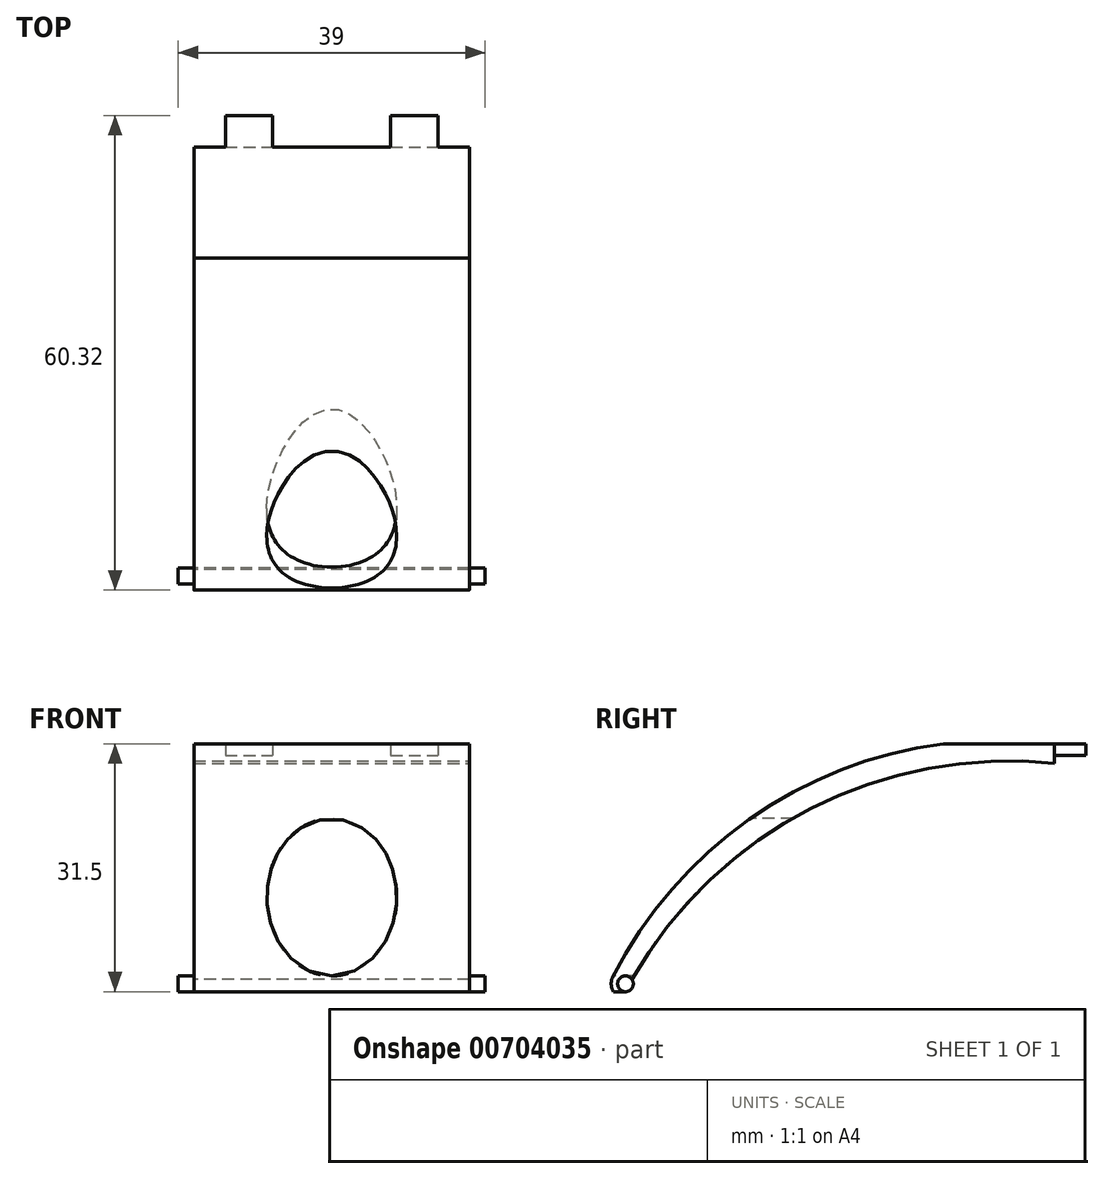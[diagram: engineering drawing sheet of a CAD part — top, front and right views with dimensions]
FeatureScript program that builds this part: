
annotation { "Feature Type Name" : "Feature", "Feature Type Description" : "" }
export const myFeature = defineFeature(function(context is Context, id is Id, definition is map)
    precondition{}
    {
        {
            var Q0;
            Q0=qCreatedBy(makeId("Top.planeOp"),FACE);
            var sketch = newSketch(context, id + "F0", { "sketchPlane" : qUnion([Q0])});
            skLineSegment(sketch, "E0.bottom", {"start": v(-17.4, 3.7) * mm, "end": v(17.6, 3.7) * mm});
            skLineSegment(sketch, "E0.top", {"start": v(-17.4, -53.3) * mm, "end": v(17.6, -53.3) * mm});
            skLineSegment(sketch, "E0.left", {"start": v(-17.4, 3.7) * mm, "end": v(-17.4, -53.3) * mm});
            skLineSegment(sketch, "E0.right", {"start": v(17.6, 3.7) * mm, "end": v(17.6, -53.3) * mm});
            skSolve(sketch);
        }
        {
            var Q0;
            Q0=makeQuery(id+"F0.imprint","IMPRINT",FACE,{"disambiguationData":[TD([[makeQuery(id+"F0.imprint","IMPRINT",EDGE,{"derivedFrom":sQuery(id+"F0.wireOp",EDGE,"E0.bottom")}),-1.0]])]});
            extrude(context, id + "F1", {"entities" : qUnion([Q0]), "depth" : 31.5 * mm, "offsetDistance" : 25 * mm});
        }
        {
            var Q0;
            Q0=makeQuery(id+"F1.opExtrude","SWEPT_FACE",FACE,{"disambiguationData":[OSD([sQuery(id+"F0.wireOp",EDGE,"E0.right")])]});
            var sketch = newSketch(context, id + "F2", { "sketchPlane" : qUnion([Q0])});
            skArc(sketch, "E1", {"start": v(3.7, 31.5) * mm, "mid": v(-29.97, 25.1) * mm, "end": v(-53.3, 0) * mm});
            skSolve(sketch);
        }
        {
            var Q0;
            Q0=makeQuery(id+"F1.opExtrude","SWEPT_FACE",FACE,{"disambiguationData":[OSD([sQuery(id+"F0.wireOp",EDGE,"E0.top")])]});
            var sketch = newSketch(context, id + "F3", { "sketchPlane" : qUnion([Q0])});
            skEllipse(sketch, "E2", {"center": v(0.1, 12) * mm, "majorRadius": 10 * mm, "minorRadius": 8.25 * mm, "majorAxis": v(0, -1)});
            skSolve(sketch);
        }
        {
            var Q0;
            Q0=makeQuery(id+"F3.imprint","IMPRINT",FACE,{"disambiguationData":[TD([[makeQuery(id+"F3.imprint","IMPRINT",EDGE,{"derivedFrom":sQuery(id+"F3.wireOp",EDGE,"E2")}),1.0]])]});
            extrude(context, id + "F4", {"entities" : qUnion([Q0]), "operationType" : NewBodyOperationType.REMOVE, "endBound" : BoundingType.THROUGH_ALL, "oppositeDirection" : true, "depth" : 25 * mm, "offsetDistance" : 25 * mm});
        }
        {
            var Q0;
            Q0=makeQuery(id+"F2.imprint","IMPRINT",FACE,{"disambiguationData":[TD([[makeQuery(id+"F2.imprint","IMPRINT",EDGE,{"derivedFrom":sQuery(id+"F2.wireOp",EDGE,"E1")}),-1.0]])]});
            extrude(context, id + "F5", {"entities" : qUnion([Q0]), "operationType" : NewBodyOperationType.REMOVE, "endBound" : BoundingType.THROUGH_ALL, "oppositeDirection" : true, "depth" : 25 * mm, "offsetDistance" : 25 * mm});
        }
        {
            var Q0;
            Q0=makeQuery(id+"F1.opExtrude","SWEPT_FACE",FACE,{"disambiguationData":[OSD([sQuery(id+"F0.wireOp",EDGE,"E0.right")])]});
            var sketch = newSketch(context, id + "F6", { "sketchPlane" : qUnion([Q0])});
            skArc(sketch, "E3", {"start": v(3.7, 29) * mm, "mid": v(-28, 22.87) * mm, "end": v(-50.8, 0) * mm});
            skSolve(sketch);
        }
        {
            var Q0;
            {var subQ0=sQuery(id+"F6.wireOp",EDGE,"E3");Q0=makeQuery(id+"F6.imprint","IMPRINT",FACE,{"disambiguationData":[TD([[makeQuery(id+"F6.imprint","IMPRINT",EDGE,{"derivedFrom":subQ0}),1.0]])]});}
            extrude(context, id + "F7", {"entities" : qUnion([Q0]), "operationType" : NewBodyOperationType.REMOVE, "endBound" : BoundingType.THROUGH_ALL, "oppositeDirection" : true, "depth" : 25 * mm, "offsetDistance" : 25 * mm});
        }
        {
            var Q0;
            Q0=makeQuery(id+"F1.opExtrude","SWEPT_FACE",FACE,{"disambiguationData":[OSD([sQuery(id+"F0.wireOp",EDGE,"E0.right")])]});
            var sketch = newSketch(context, id + "F8", { "sketchPlane" : qUnion([Q0])});
            skCircle(sketch, "E4", {"center": v(-50.8, 1) * mm, "radius": 1 * mm});
            skSolve(sketch);
        }
        {
            var Q0;
            {var subQ0=sQuery(id+"F8.wireOp",EDGE,"E4");var subQ1=makeQuery(id+"F7.boolean.opBoolean","COPY",EDGE,{"derivedFrom":makeQuery(id+"F7.opExtrude","CAP_EDGE",EDGE,{"disambiguationData":[OSD([sQuery(id+"F6.wireOp",EDGE,"E3")])],"isStart":true})});var subQ3=makeQuery(id+"F8.imprint","INTERSECT",VERTEX,{"derivedFrom":[subQ1,subQ0]});Q0=makeQuery(id+"F8.imprint","IMPRINT",FACE,{"disambiguationData":[TD([[makeQuery(id+"F8.imprint","IMPRINT",EDGE,{"disambiguationData":[TD([[subQ3,-1.0]])],"derivedFrom":subQ0}),1.0]])]});}
            var Q1;
            {var subQ0=sQuery(id+"F8.wireOp",EDGE,"E4");var subQ1=makeQuery(id+"F7.boolean.opBoolean","COPY",EDGE,{"derivedFrom":makeQuery(id+"F7.opExtrude","CAP_EDGE",EDGE,{"disambiguationData":[OSD([sQuery(id+"F6.wireOp",EDGE,"E3")])],"isStart":true})});var subQ3=makeQuery(id+"F8.imprint","INTERSECT",VERTEX,{"derivedFrom":[subQ1,subQ0]});Q1=makeQuery(id+"F8.imprint","IMPRINT",FACE,{"disambiguationData":[TD([[makeQuery(id+"F8.imprint","IMPRINT",EDGE,{"disambiguationData":[TD([[subQ3,1.0]])],"derivedFrom":subQ0}),1.0]])]});}
            extrude(context, id + "F9", {"entities" : qUnion([Q0, Q1]), "operationType" : NewBodyOperationType.ADD, "depth" : 2 * mm, "offsetDistance" : 25 * mm, "hasSecondDirection" : true, "secondDirectionOppositeDirection" : true, "secondDirectionDepth" : 37 * mm});
        }
        {
            var Q0;
            Q0=makeQuery(id+"F1.opExtrude","SWEPT_FACE",FACE,{"disambiguationData":[OSD([sQuery(id+"F0.wireOp",EDGE,"E0.right")])]});
            var sketch = newSketch(context, id + "F10", { "sketchPlane" : qUnion([Q0])});
            skCircle(sketch, "E5", {"center": v(-50.8, 1) * mm, "radius": 1.82 * mm});
            skSolve(sketch);
        }
        {
            var Q0;
            {var subQ0=sQuery(id+"F10.wireOp",EDGE,"E5");var subQ1=makeQuery(id+"F5.boolean.opBoolean","COPY",EDGE,{"derivedFrom":makeQuery(id+"F5.opExtrude","CAP_EDGE",EDGE,{"disambiguationData":[OSD([sQuery(id+"F2.wireOp",EDGE,"E1")])],"isStart":true})});var subQ2=makeQuery(id+"F10.imprint","INTERSECT",VERTEX,{"derivedFrom":[subQ1,subQ0]});Q0=makeQuery(id+"F10.imprint","IMPRINT",FACE,{"disambiguationData":[TD([[makeQuery(id+"F10.imprint","IMPRINT",EDGE,{"disambiguationData":[TD([[subQ2,-1.0]])],"derivedFrom":subQ0}),-1.0]])]});}
            extrude(context, id + "F11", {"entities" : qUnion([Q0]), "operationType" : NewBodyOperationType.REMOVE, "endBound" : BoundingType.THROUGH_ALL, "oppositeDirection" : true, "depth" : 25 * mm, "offsetDistance" : 25 * mm});
        }
        {
            var Q0;
            Q0=makeQuery(id+"F1.opExtrude","SWEPT_FACE",FACE,{"disambiguationData":[OSD([sQuery(id+"F0.wireOp",EDGE,"E0.bottom")])]});
            var sketch = newSketch(context, id + "F12", { "sketchPlane" : qUnion([Q0])});
            skLineSegment(sketch, "E6.bottom", {"start": v(-13.6, 31.5) * mm, "end": v(-7.6, 31.5) * mm});
            skLineSegment(sketch, "E6.top", {"start": v(-13.6, 29) * mm, "end": v(-7.6, 29) * mm});
            skLineSegment(sketch, "E6.left", {"start": v(-13.6, 31.5) * mm, "end": v(-13.6, 29) * mm});
            skLineSegment(sketch, "E6.right", {"start": v(-7.6, 31.5) * mm, "end": v(-7.6, 29) * mm});
            skLineSegment(sketch, "E7.bottom", {"start": v(7.4, 31.5) * mm, "end": v(13.4, 31.5) * mm});
            skLineSegment(sketch, "E7.top", {"start": v(7.4, 29) * mm, "end": v(13.4, 29) * mm});
            skLineSegment(sketch, "E7.left", {"start": v(7.4, 31.5) * mm, "end": v(7.4, 29) * mm});
            skLineSegment(sketch, "E7.right", {"start": v(13.4, 31.5) * mm, "end": v(13.4, 29) * mm});
            skSolve(sketch);
        }
        {
            var Q0;
            Q0=makeQuery(id+"F12.imprint","IMPRINT",FACE,{"disambiguationData":[TD([[makeQuery(id+"F12.imprint","IMPRINT",EDGE,{"derivedFrom":sQuery(id+"F12.wireOp",EDGE,"E6.bottom")}),1.0]])]});
            var Q1;
            Q1=makeQuery(id+"F12.imprint","IMPRINT",FACE,{"disambiguationData":[TD([[makeQuery(id+"F12.imprint","IMPRINT",EDGE,{"derivedFrom":sQuery(id+"F12.wireOp",EDGE,"E7.bottom")}),1.0]])]});
            extrude(context, id + "F13", {"entities" : qUnion([Q0, Q1]), "operationType" : NewBodyOperationType.ADD, "depth" : 4 * mm, "offsetDistance" : 25 * mm});
        }
        {
            var Q0;
            Q0=makeQuery(id+"F13.opExtrude","SWEPT_FACE",FACE,{"disambiguationData":[OSD([sQuery(id+"F12.wireOp",EDGE,"E6.top")])]});
            var Q1;
            Q1=makeQuery(id+"F13.opExtrude","SWEPT_FACE",FACE,{"disambiguationData":[OSD([sQuery(id+"F12.wireOp",EDGE,"E7.top")])]});
            extrude(context, id + "F14", {"entities" : qUnion([Q0, Q1]), "operationType" : NewBodyOperationType.REMOVE, "oppositeDirection" : true, "depth" : 1 * mm, "offsetDistance" : 25 * mm});
        }
    });
